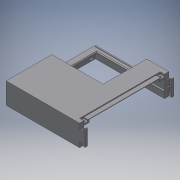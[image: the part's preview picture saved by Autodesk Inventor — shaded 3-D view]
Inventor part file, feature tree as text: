
AUTODESK INVENTOR PART (.ipt)
format: ipt  version: 2016 SP2 (Build 200236200, 236)  size: 831,488 bytes
history: native  units: mm
features: sketch x25, other x5
ambient origin geometry x8: Origin, YZ Plane, XZ Plane, XY Plane, X Axis, Y Axis, Z Axis, Center Point
bodies: Volumenkörper1 (feature_tree), Volumenkörper2 (feature_tree), Volumenkörper3 (feature_tree)
feature tree (30):
  other  "Case_side_back_MIR.ipt"
  other  "Volumenkörper1::Case_side_back_MIR.ipt"
  other  "Volumenkörper2::Case_side_back_MIR.ipt"
  other  "Volumenkörper3::Case_side_back_MIR.ipt"
  other  "Bezeichnung1"
  sketch  "Skizze1"  dims[d0=10.0mm]
  sketch  "Skizze2"
  sketch  "Skizze3"
  sketch  "Skizze4"
  sketch  "Skizze6"
  sketch  "Skizze7"
  sketch  "Skizze8"
  sketch  "Skizze9"
  sketch  "Skizze10"
  sketch  "Skizze11"
  sketch  "Skizze12"
  sketch  "Skizze13"
  sketch  "Skizze14"
  sketch  "Skizze15"
  sketch  "Skizze16"
  sketch  "Skizze17"
  sketch  "Skizze18"
  sketch  "Skizze19"
  sketch  "Skizze20"
  sketch  "Skizze21"
  sketch  "Skizze22"
  sketch  "Skizze23"
  sketch  "Skizze24"
  sketch  "Skizze25"
  sketch  "Skizze26"
